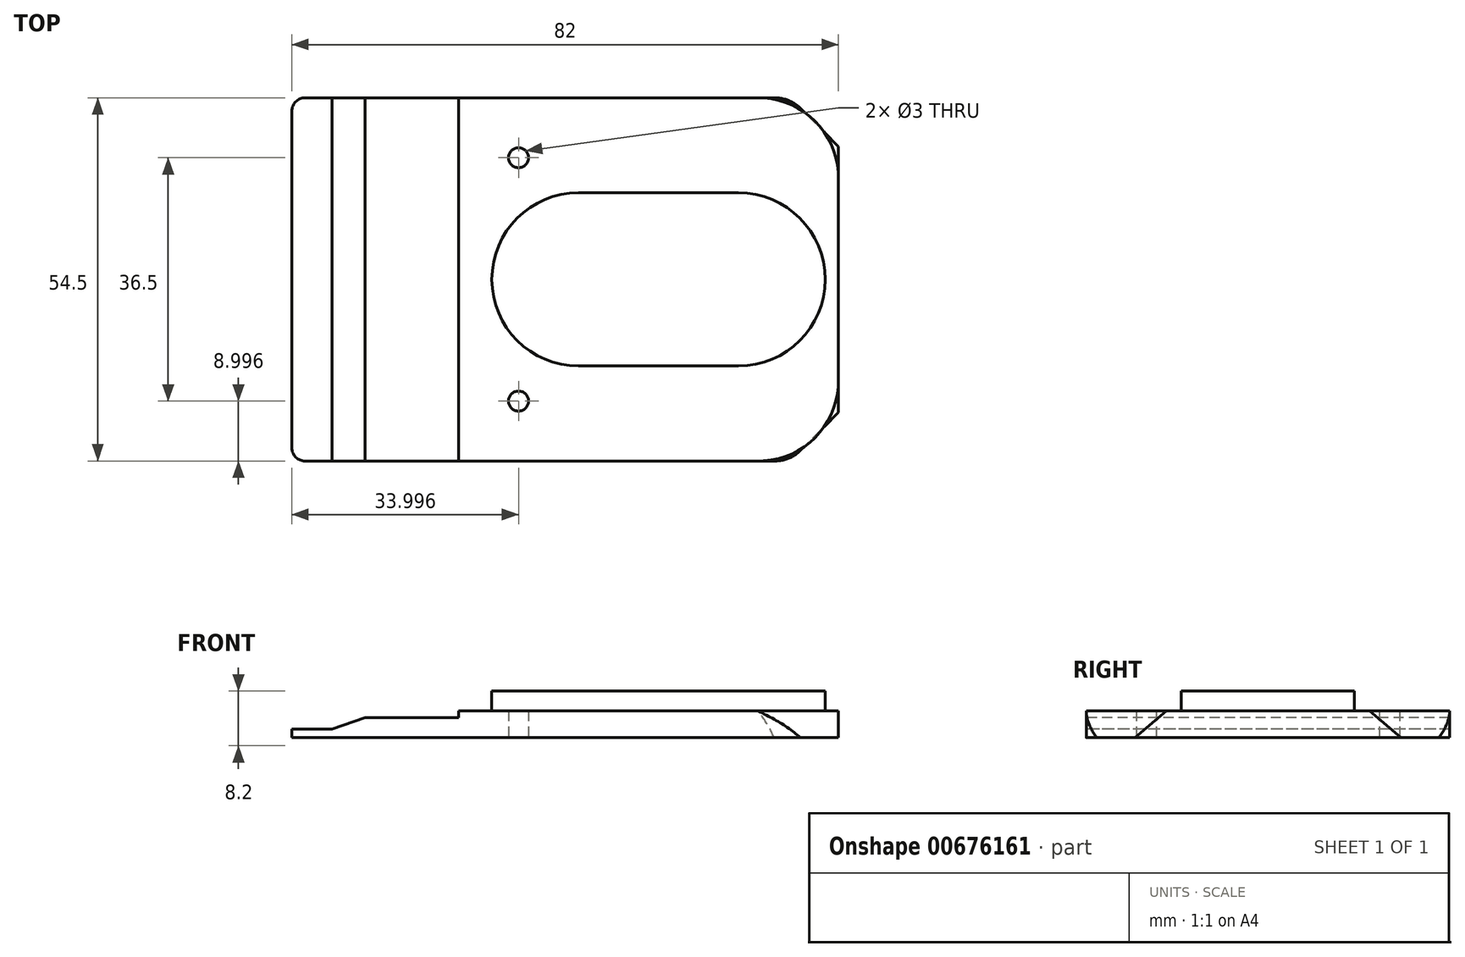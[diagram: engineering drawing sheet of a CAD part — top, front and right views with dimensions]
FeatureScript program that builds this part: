
annotation { "Feature Type Name" : "Feature", "Feature Type Description" : "" }
export const myFeature = defineFeature(function(context is Context, id is Id, definition is map)
    precondition{}
    {
        {
            var Q0;
            Q0=qCreatedBy(makeId("Top.planeOp"),FACE);
            var sketch = newSketch(context, id + "F0", { "sketchPlane" : qUnion([Q0])});
            skLineSegment(sketch, "E0.bottom", {"start": v(-44.32, 20.16) * mm, "end": v(30.38, 20.16) * mm});
            skLineSegment(sketch, "E0.top", {"start": v(-44.32, -34.34) * mm, "end": v(30.38, -34.34) * mm});
            skLineSegment(sketch, "E0.left", {"start": v(-44.32, 20.16) * mm, "end": v(-44.32, -34.34) * mm});
            skLineSegment(sketch, "E0.right", {"start": v(37.68, 12.86) * mm, "end": v(37.68, -27.04) * mm});
            skPoint(sketch, "E1.visualSharp", {"position": v(37.68, 20.16) * mm});
            skPoint(sketch, "E2.visualSharp", {"position": v(37.68, -34.34) * mm});
            skLineSegment(sketch, "E3", {"start": v(-38.32, 20.16) * mm, "end": v(-38.32, -34.34) * mm});
            skLineSegment(sketch, "E4", {"start": v(-19.32, 20.16) * mm, "end": v(-19.32, -34.34) * mm});
            skLineSegment(sketch, "E5", {"start": v(30.38, 20.16) * mm, "end": v(37.68, 12.86) * mm});
            skLineSegment(sketch, "E6", {"start": v(37.68, -27.04) * mm, "end": v(30.38, -34.34) * mm});
            skSolve(sketch);
        }
        {
            assignVariable(context, id + "F1", {"name" : "h", "anyValue" : 4});
        }
        {
            var Q0;
            Q0=qCreatedBy(makeId("Top.planeOp"),FACE);
            cPlane(context, id + "F2", {"entities" : qUnion([Q0]), "cplaneType" : CPlaneType.OFFSET, "offset" : (getVariable(context, 'h')) * mm, "width" : 150 * mm, "height" : 150 * mm});
        }
        {
            var Q0;
            Q0=qCreatedBy(id+"F2.planeOp",FACE);
            var sketch = newSketch(context, id + "F3", { "sketchPlane" : qUnion([Q0])});
            skLineSegment(sketch, "E7.0", {"start": v(-44.32, 20.16) * mm, "end": v(25.68, 20.16) * mm});
            skLineSegment(sketch, "E8.0", {"start": v(-19.32, 20.16) * mm, "end": v(-19.32, -34.34) * mm});
            skLineSegment(sketch, "E9.0", {"start": v(37.68, 8.16) * mm, "end": v(37.68, -27.04) * mm});
            skLineSegment(sketch, "E10.0", {"start": v(-44.32, -34.34) * mm, "end": v(30.38, -34.34) * mm});
            skLineSegment(sketch, "E11", {"start": v(25.68, -34.34) * mm, "end": v(30.38, -34.34) * mm});
            skLineSegment(sketch, "E12", {"start": v(37.68, -27.04) * mm, "end": v(37.68, -22.34) * mm});
            skPoint(sketch, "E13.visualSharp", {"position": v(37.68, -34.34) * mm});
            skArc(sketch, "E13.filletArc", {"start": v(25.68, -34.34) * mm, "mid": v(34.16, -30.83) * mm, "end": v(37.68, -22.34) * mm});
            skPoint(sketch, "E14.newPointA", {"position": v(30.38, 20.16) * mm});
            skPoint(sketch, "E14.newPointB", {"position": v(37.68, 12.86) * mm});
            skArc(sketch, "E14.filletArc", {"start": v(37.68, 8.16) * mm, "mid": v(34.16, 16.64) * mm, "end": v(25.68, 20.16) * mm});
            skSolve(sketch);
        }
        {
            var Q0;
            Q0=makeQuery(id+"F0.imprint","IMPRINT",FACE,{"disambiguationData":[TD([[makeQuery(id+"F0.imprint","IMPRINT",EDGE,{"derivedFrom":sQuery(id+"F0.wireOp",EDGE,"E0.right")}),-1.0]])]});
            var Q1;
            {var subQ1=sQuery(id+"F3.wireOp",EDGE,"E8.0");Q1=makeQuery(id+"F3.imprint","IMPRINT",FACE,{"disambiguationData":[TD([[makeQuery(id+"F3.imprint","IMPRINT",EDGE,{"derivedFrom":subQ1}),1.0]])]});}
            loft(context, id + "F4", {"sheetProfilesArray" : [{ "sheetProfileEntities" : qUnion([Q0]) }, { "sheetProfileEntities" : qUnion([Q1]) }]});
        }
        {
            var Q0;
            {var subQ0=sQuery(id+"F0.wireOp",EDGE,"E3");Q0=makeQuery(id+"F0.imprint","IMPRINT",FACE,{"disambiguationData":[TD([[makeQuery(id+"F0.imprint","IMPRINT",EDGE,{"derivedFrom":subQ0}),1.0]])]});}
            extrude(context, id + "F5", {"entities" : qUnion([Q0]), "operationType" : NewBodyOperationType.ADD, "depth" : (getVariable(context, 'h') - 1) * mm, "offsetDistance" : 25 * mm});
        }
        {
            var Q0;
            {var subQ0=sQuery(id+"F0.wireOp",EDGE,"E0.left");Q0=makeQuery(id+"F0.imprint","IMPRINT",FACE,{"disambiguationData":[TD([[makeQuery(id+"F0.imprint","IMPRINT",EDGE,{"derivedFrom":subQ0}),1.0]])]});}
            extrude(context, id + "F6", {"entities" : qUnion([Q0]), "operationType" : NewBodyOperationType.ADD, "depth" : (getVariable(context, 'h') - 1 - 1.7) * mm, "offsetDistance" : 25 * mm});
        }
        {
            var Q0;
            Q0=makeQuery(id+"F5.opExtrude","CAP_EDGE",EDGE,{"disambiguationData":[OSD([sQuery(id+"F0.wireOp",EDGE,"E3")])],"isStart":false});
            chamfer(context, id + "F7", {"entities" : qUnion([Q0]), "chamferType" : ChamferType.TWO_OFFSETS, "width1" : 5 * mm, "oppositeDirection" : false, "width2" : 1.7 * mm, "tangentPropagation" : true});
        }
        {
            var Q0;
            Q0=qCreatedBy(makeId("Top.planeOp"),FACE);
            var sketch = newSketch(context, id + "F8", { "sketchPlane" : qUnion([Q0])});
            skLineSegment(sketch, "E15.0.1", {"start": v(-19.32, 20.16) * mm, "end": v(-19.32, -34.34) * mm});
            skLineSegment(sketch, "E16.bottom", {"start": v(22.68, 5.9) * mm, "end": v(-1.32, 5.9) * mm});
            skLineSegment(sketch, "E16.top", {"start": v(22.68, -20.1) * mm, "end": v(-1.32, -20.1) * mm});
            skLineSegment(sketch, "E16.left", {"start": v(35.68, -7.1) * mm, "end": v(35.68, -7.1) * mm});
            skLineSegment(sketch, "E16.right", {"start": v(-14.32, -7.1) * mm, "end": v(-14.32, -7.1) * mm});
            skPoint(sketch, "E17.visualSharp", {"position": v(35.68, 5.9) * mm});
            skArc(sketch, "E17.filletArc", {"start": v(35.68, -7.1) * mm, "mid": v(31.87, 2.1) * mm, "end": v(22.68, 5.9) * mm});
            skPoint(sketch, "E18.visualSharp", {"position": v(35.68, -20.1) * mm});
            skArc(sketch, "E18.filletArc", {"start": v(22.68, -20.1) * mm, "mid": v(31.87, -16.29) * mm, "end": v(35.68, -7.1) * mm});
            skPoint(sketch, "E19.visualSharp", {"position": v(-14.32, -20.1) * mm});
            skArc(sketch, "E19.filletArc", {"start": v(-14.32, -7.1) * mm, "mid": v(-10.52, -16.29) * mm, "end": v(-1.32, -20.1) * mm});
            skArc(sketch, "E20.filletArc", {"start": v(-1.32, 5.9) * mm, "mid": v(-10.52, 2.1) * mm, "end": v(-14.32, -7.1) * mm});
            skLineSegment(sketch, "E21.0.1", {"start": v(-19.32, 20.16) * mm, "end": v(-19.32, 20.16) * mm});
            skLineSegment(sketch, "E21.0.4", {"start": v(37.68, 8.16) * mm, "end": v(37.68, 8.16) * mm});
            skSolve(sketch);
        }
        {
            var Q0;
            Q0=makeQuery(id+"F8.imprint","IMPRINT",FACE,{"disambiguationData":[TD([[makeQuery(id+"F8.imprint","IMPRINT",EDGE,{"derivedFrom":sQuery(id+"F8.wireOp",EDGE,"E16.top")}),-1.0]])]});
            extrude(context, id + "F9", {"entities" : qUnion([Q0]), "operationType" : NewBodyOperationType.ADD, "depth" : (getVariable(context, 'h') + 3) * mm, "offsetDistance" : 25 * mm});
        }
        {
            var Q0;
            Q0=makeQuery(id+"F6.opExtrude","SWEPT_EDGE",EDGE,{"disambiguationData":[OSD([sQuery(id+"F0.wireOp",EDGE,"E0.bottom"),sQuery(id+"F0.wireOp",EDGE,"E0.left")])]});
            var Q1;
            Q1=makeQuery(id+"F6.opExtrude","SWEPT_EDGE",EDGE,{"disambiguationData":[OSD([sQuery(id+"F0.wireOp",EDGE,"E0.top"),sQuery(id+"F0.wireOp",EDGE,"E0.left")])]});
            fillet(context, id + "F10", {"entities" : qUnion([Q0, Q1]), "radius" : 2 * mm, "tangentPropagation" : true, "allowEdgeOverflow" : false});
        }
        {
            var Q0;
            Q0=makeQuery(id+"F4.opLoft","SWEPT_EDGE",EDGE,{"disambiguationData":[OSD([sQuery(id+"F0.wireOp",EDGE,"E0.top"),sQuery(id+"F0.wireOp",EDGE,"E6"),sQuery(id+"F3.wireOp",EDGE,"0376f334-68b6-4604-9fff-a22471a253ce.0"),sQuery(id+"F3.wireOp",EDGE,"GD4RCVqp-BcxK-n8Ms-Y5Tf-ogGmLrL9diAB")])]});
            var Q1;
            Q1=makeQuery(id+"F4.opLoft","SWEPT_EDGE",EDGE,{"disambiguationData":[OSD([sQuery(id+"F0.wireOp",EDGE,"E0.bottom"),sQuery(id+"F0.wireOp",EDGE,"E5"),sQuery(id+"F3.wireOp",EDGE,"E7.0"),sQuery(id+"F3.wireOp",EDGE,"3XW9bA0Z-Y5q1-Bp0y-vJFE-kiWpjOHeechs")])]});
            fillet(context, id + "F11", {"entities" : qUnion([Q0, Q1]), "radius" : 5 * mm, "tangentPropagation" : true, "allowEdgeOverflow" : false});
        }
        {
            var Q0;
            Q0=qCreatedBy(makeId("Top.planeOp"),FACE);
            var sketch = newSketch(context, id + "F12", { "sketchPlane" : qUnion([Q0])});
            skLineSegment(sketch, "E22.0", {"start": v(-44.32, -34.34) * mm, "end": v(30.38, -34.34) * mm});
            skLineSegment(sketch, "E23.0", {"start": v(-44.32, 20.16) * mm, "end": v(30.38, 20.16) * mm});
            skLineSegment(sketch, "E24.0", {"start": v(37.68, 12.86) * mm, "end": v(37.68, -27.04) * mm});
            skCircle(sketch, "E25", {"center": v(-10.32, -25.34) * mm, "radius": 1.5 * mm});
            skCircle(sketch, "E26", {"center": v(-10.32, 11.16) * mm, "radius": 1.5 * mm});
            skSolve(sketch);
        }
        {
            var Q0;
            Q0=makeQuery(id+"F12.imprint","IMPRINT",FACE,{"disambiguationData":[TD([[makeQuery(id+"F12.imprint","IMPRINT",EDGE,{"derivedFrom":sQuery(id+"F12.wireOp",EDGE,"E25")}),1.0]])]});
            var Q1;
            Q1=makeQuery(id+"F12.imprint","IMPRINT",FACE,{"disambiguationData":[TD([[makeQuery(id+"F12.imprint","IMPRINT",EDGE,{"derivedFrom":sQuery(id+"F12.wireOp",EDGE,"E26")}),1.0]])]});
            extrude(context, id + "F13", {"entities" : qUnion([Q0, Q1]), "operationType" : NewBodyOperationType.REMOVE, "depth" : 25 * mm, "offsetDistance" : 25 * mm});
        }
    });
